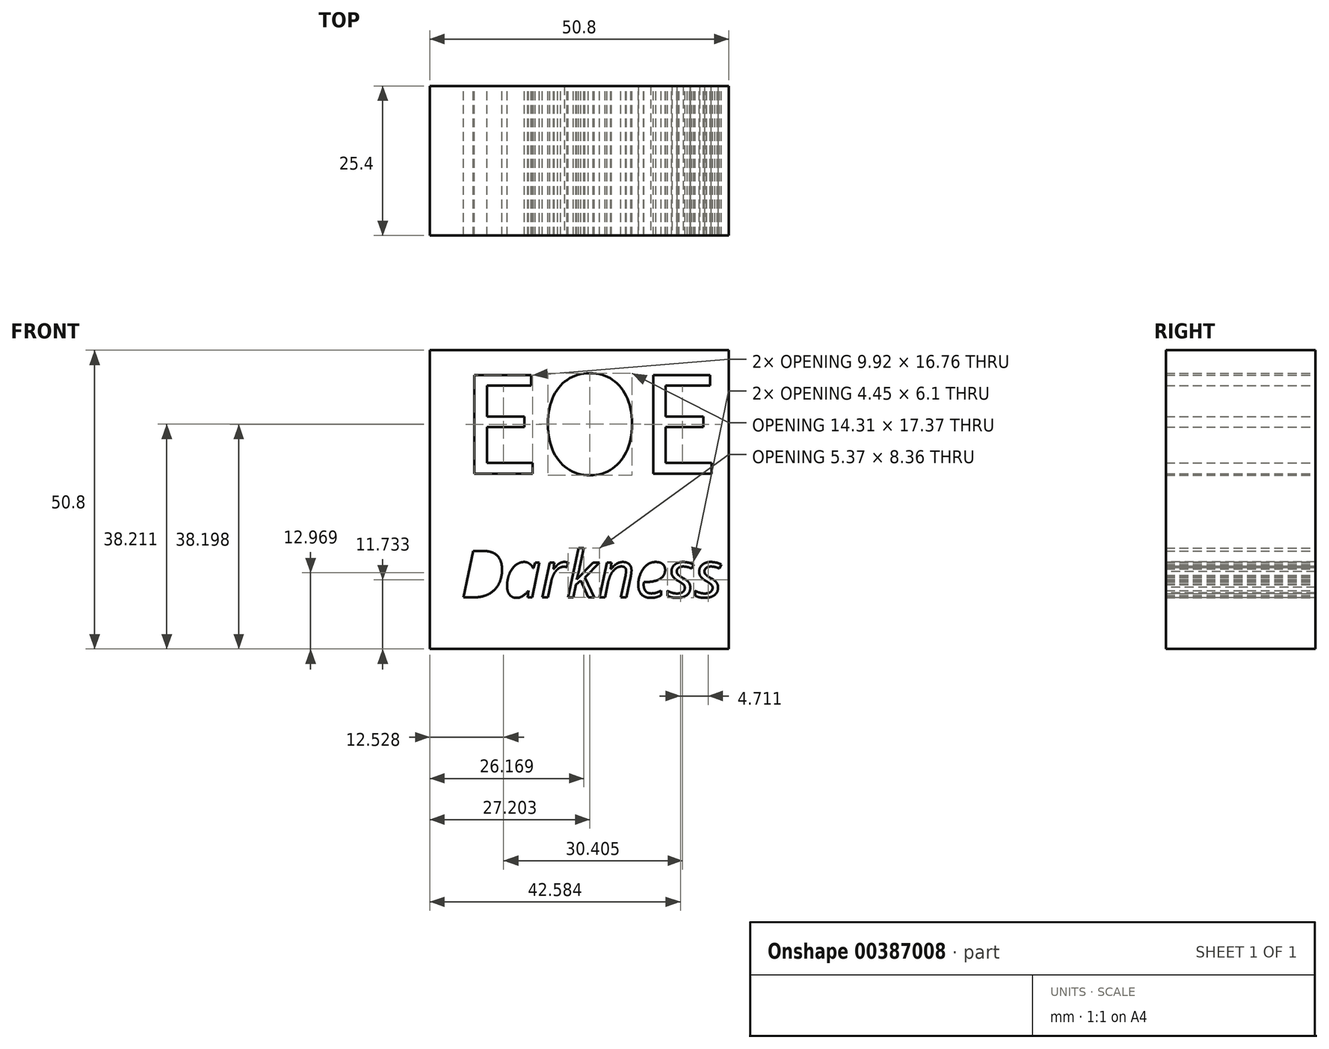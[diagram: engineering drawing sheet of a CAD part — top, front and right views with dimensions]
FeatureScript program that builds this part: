
annotation { "Feature Type Name" : "Feature", "Feature Type Description" : "" }
export const myFeature = defineFeature(function(context is Context, id is Id, definition is map)
    precondition{}
    {
        {
            var Q0;
            Q0=qCreatedBy(makeId("Front.planeOp"),FACE);
            var sketch = newSketch(context, id + "F0", { "sketchPlane" : qUnion([Q0])});
            skLineSegment(sketch, "E0.bottom", {"start": v(25.4, 25.4) * mm, "end": v(-25.4, 25.4) * mm});
            skLineSegment(sketch, "E0.top", {"start": v(25.4, -25.4) * mm, "end": v(-25.4, -25.4) * mm});
            skLineSegment(sketch, "E0.left", {"start": v(25.4, 25.4) * mm, "end": v(25.4, -25.4) * mm});
            skLineSegment(sketch, "E0.right", {"start": v(-25.4, 25.4) * mm, "end": v(-25.4, -25.4) * mm});
            skPoint(sketch, "E0.middle", {"position": v(0, 0) * mm});
            skText(sketch, "E1", { "text": "EOE", "fontName": "NotoSansCJKjp-Regular.otf"});
            skText(sketch, "E2", { "text": "Darkness", "fontName": "OpenSans-Italic.ttf"});
            const initialGuessF0  = {"E1": [-0.02012, 0.00442, 1, 0, 0.01646], "E2": [-0.02012, -0.01661, 1, 0, 0.00792]};
            skSetInitialGuess(sketch, initialGuessF0);
            skSolve(sketch);
        }
        {
            var Q0;
            Q0=makeQuery(id+"F0.imprint","IMPRINT",FACE,{"disambiguationData":[TD([[makeQuery(id+"F0.imprint","IMPRINT",EDGE,{"derivedFrom":sQuery(id+"F0.wireOp",EDGE,"E0.bottom")}),1.0]])]});
            extrude(context, id + "F1", {"entities" : qUnion([Q0]), "depth" : 25.4 * mm});
        }
    });
